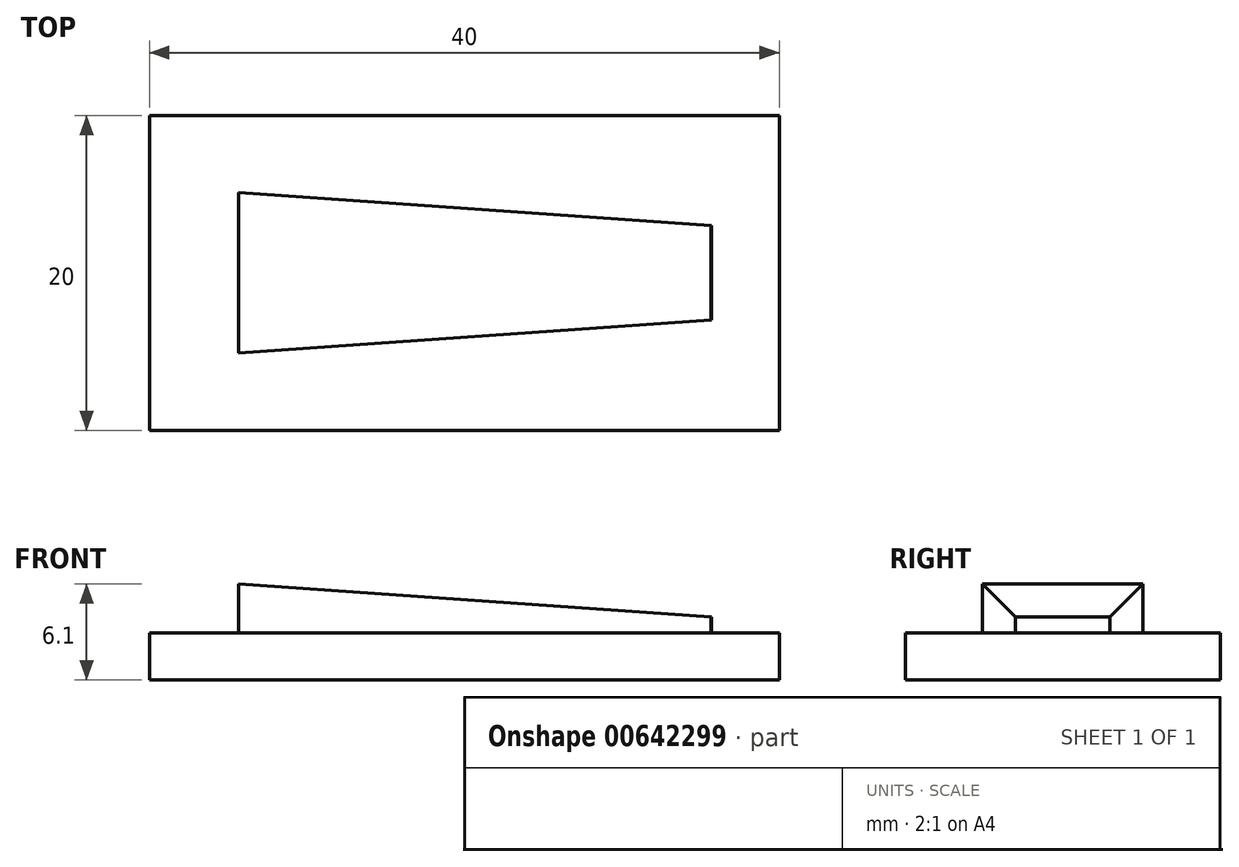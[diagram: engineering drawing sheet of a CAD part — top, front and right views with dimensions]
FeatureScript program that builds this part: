
annotation { "Feature Type Name" : "Feature", "Feature Type Description" : "" }
export const myFeature = defineFeature(function(context is Context, id is Id, definition is map)
    precondition{}
    {
        {
            var Q0;
            Q0=qCreatedBy(makeId("Top.planeOp"),FACE);
            var sketch = newSketch(context, id + "F0", { "sketchPlane" : qUnion([Q0])});
            skLineSegment(sketch, "E0.bottom", {"start": v(20, 10) * mm, "end": v(-20, 10) * mm});
            skLineSegment(sketch, "E0.top", {"start": v(20, -10) * mm, "end": v(-20, -10) * mm});
            skLineSegment(sketch, "E0.left", {"start": v(20, 10) * mm, "end": v(20, -10) * mm});
            skLineSegment(sketch, "E0.right", {"start": v(-20, 10) * mm, "end": v(-20, -10) * mm});
            skPoint(sketch, "E0.middle", {"position": v(0, 0) * mm});
            skSolve(sketch);
        }
        {
            var Q0;
            Q0=makeQuery(id+"F0.imprint","IMPRINT",FACE,{"disambiguationData":[TD([[makeQuery(id+"F0.imprint","IMPRINT",EDGE,{"derivedFrom":sQuery(id+"F0.wireOp",EDGE,"E0.bottom")}),1.0]])]});
            extrude(context, id + "F1", {"entities" : qUnion([Q0]), "depth" : 3 * mm, "offsetDistance" : 25 * mm});
        }
        {
            var Q0;
            Q0=makeQuery(id+"F1.opExtrude","CAP_FACE",FACE,{"disambiguationData":[OSD([sQuery(id+"F0.wireOp",EDGE,"E0.bottom"),sQuery(id+"F0.wireOp",EDGE,"E0.top"),sQuery(id+"F0.wireOp",EDGE,"E0.left"),sQuery(id+"F0.wireOp",EDGE,"E0.right")])],"isStart":false});
            var sketch = newSketch(context, id + "F2", { "sketchPlane" : qUnion([Q0])});
            skLineSegment(sketch, "E1.bottom", {"start": v(15.7, -3) * mm, "end": v(15.65, -3) * mm});
            skLineSegment(sketch, "E1.top", {"start": v(15.7, 3) * mm, "end": v(15.65, 3) * mm});
            skLineSegment(sketch, "E1.left", {"start": v(15.7, -3) * mm, "end": v(15.7, 3) * mm});
            skLineSegment(sketch, "E1.right", {"start": v(15.65, -3) * mm, "end": v(15.65, 3) * mm});
            skPoint(sketch, "E1.middle", {"position": v(15.67, 0) * mm});
            skSolve(sketch);
        }
        {
            var Q0;
            Q0=makeQuery(id+"F2.imprint","IMPRINT",FACE,{"disambiguationData":[TD([[makeQuery(id+"F2.imprint","IMPRINT",EDGE,{"derivedFrom":sQuery(id+"F2.wireOp",EDGE,"E1.bottom")}),-1.0]])]});
            extrude(context, id + "F3", {"entities" : qUnion([Q0]), "operationType" : NewBodyOperationType.ADD, "depth" : 1 * mm, "offsetDistance" : 25 * mm});
        }
        {
            var Q0;
            Q0=makeQuery(id+"F3.opExtrude","SWEPT_FACE",FACE,{"disambiguationData":[OSD([sQuery(id+"F2.wireOp",EDGE,"E1.right")])]});
            extrude(context, id + "F4", {"entities" : qUnion([Q0]), "operationType" : NewBodyOperationType.ADD, "depth" : 30 * mm, "offsetDistance" : 25 * mm, "hasDraft" : true, "draftAngle" : 4 * degree});
        }
    });
